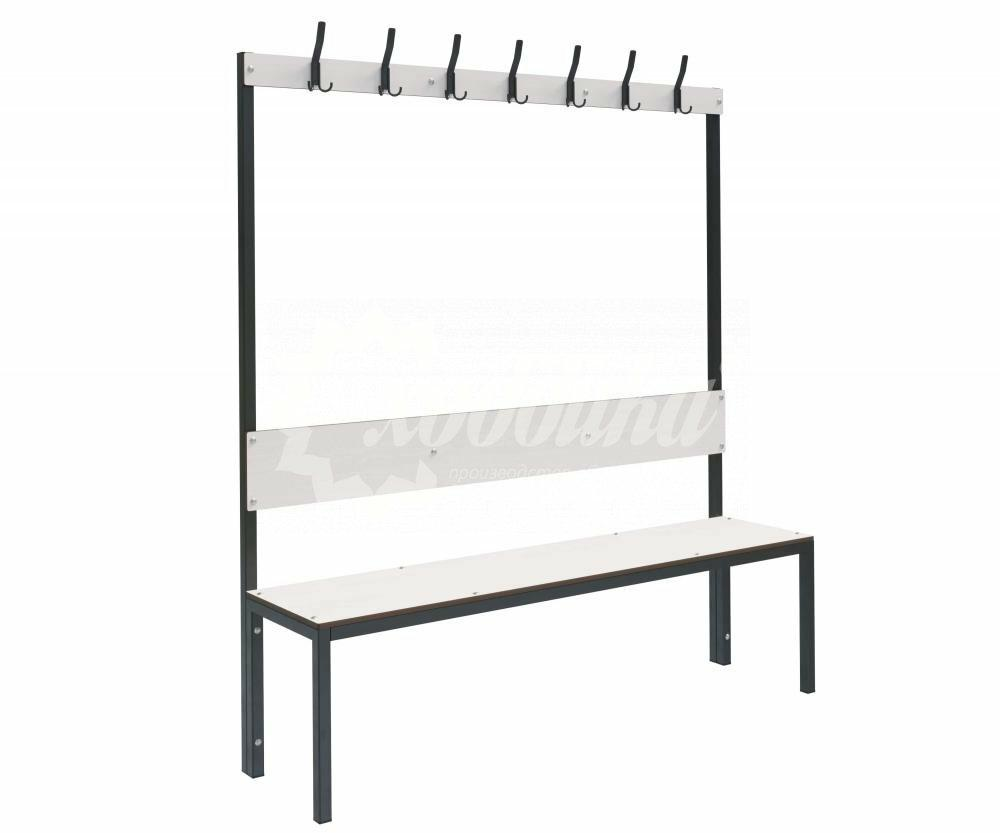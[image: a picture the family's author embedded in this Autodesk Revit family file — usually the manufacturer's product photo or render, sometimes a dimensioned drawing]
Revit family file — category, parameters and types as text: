
# Revit family: Скамейка с вешалкой для раздевалок «Фортран» Арт 20742
name_source: partatom
category: Антураж
revit_build: Autodesk Revit 2018 (Build: 20180423_1000(x64)
units: mm (PartAtom-declared; Revit-internal decimal feet)

## family parameters
Всегда вертикально = Да
Источник визуального образа = Геометрия семейства
На основе рабочей плоскости = Нет
Общий = Нет
При загрузке вырезать с полостями = Нет
Точка расчета площади = Нет

## types (2) — shared parameters
URL = https://hobbyka.ru
Артикул товара = Арт. 20742
Высота = 1650 мм
Группа модели = Скамейки для раздевалок
Изготовитель = ООО «Хоббика»
Изображение типоразмера = Скамейка с вешалкой для раздевалок «Фортран» Арт 20742.jpg
Материал изделия = Сталь, настил HPL панели
Цвет лавки = Настил HPL панели
Цвет опор = Сталь
Ширина = 380 мм

## per-type parameters (varying)
| type | Версия 1,2 м | Версия 1,5 м | Длина | Кол-во крючков | Описание |
| Версия 1,2 м | Да | Нет | 1200 мм | 5 | Скамейка с вешалкой для раздевалок «Фортран». Версия 1,2 м |
| Версия 1,5 м | Нет | Да | 1500 мм | 7 | Скамейка с вешалкой для раздевалок «Фортран». Версия 1,5 м |
